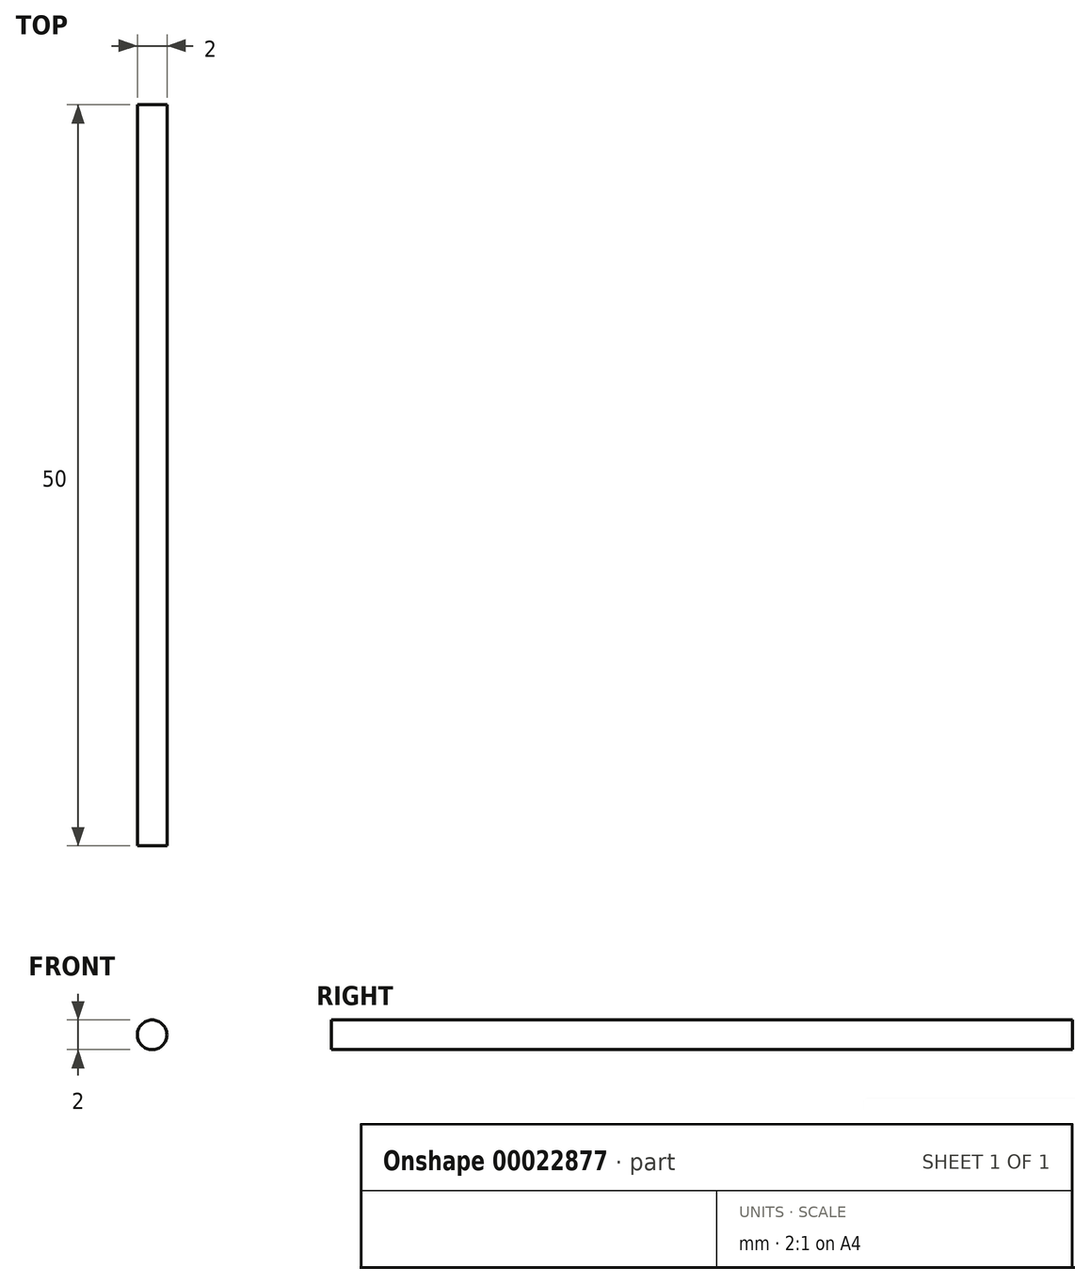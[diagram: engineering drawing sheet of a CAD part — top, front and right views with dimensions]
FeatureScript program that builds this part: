
annotation { "Feature Type Name" : "Feature", "Feature Type Description" : "" }
export const myFeature = defineFeature(function(context is Context, id is Id, definition is map)
    precondition{}
    {
        {
            var Q0;
            Q0=qCreatedBy(makeId("Front.planeOp"),FACE);
            var sketch = newSketch(context, id + "F0", { "sketchPlane" : qUnion([Q0])});
            skCircle(sketch, "E0", {"center": v(0, 0) * mm, "radius": 1 * mm});
            skSolve(sketch);
        }
        {
            var Q0;
            Q0=makeQuery(id+"F0.imprint","IMPRINT",FACE,{"disambiguationData":[TD([[makeQuery(id+"F0.imprint","IMPRINT",EDGE,{"derivedFrom":sQuery(id+"F0.wireOp",EDGE,"E0")}),1.0]])]});
            extrude(context, id + "F1", {"entities" : qUnion([Q0]), "endBound" : BoundingType.SYMMETRIC, "depth" : 50 * mm});
        }
    });
